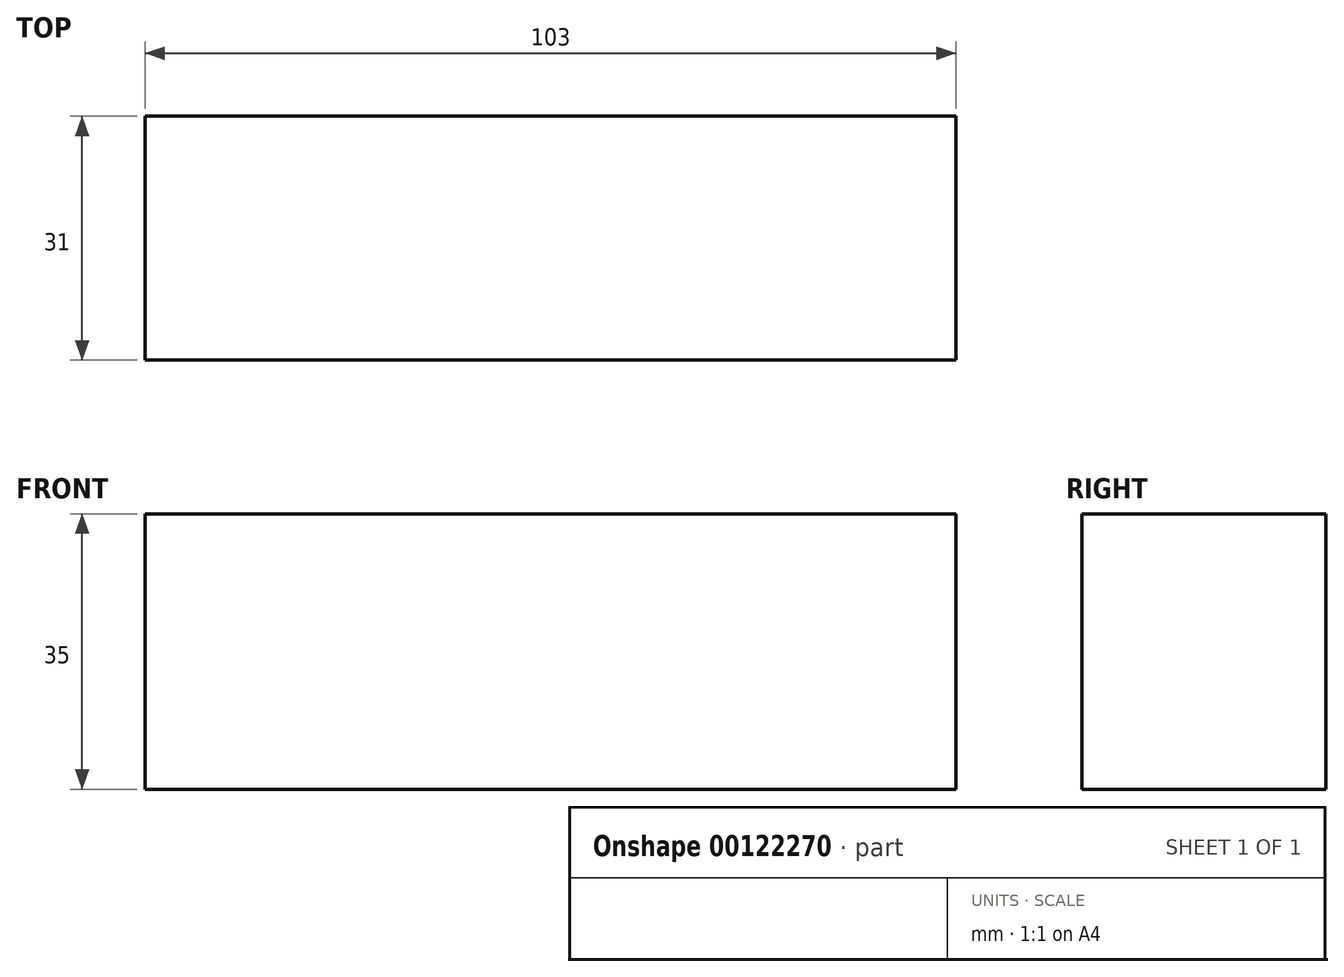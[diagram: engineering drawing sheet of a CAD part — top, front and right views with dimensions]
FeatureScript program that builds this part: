
annotation { "Feature Type Name" : "Feature", "Feature Type Description" : "" }
export const myFeature = defineFeature(function(context is Context, id is Id, definition is map)
    precondition{}
    {
        {
            var Q0;
            Q0=qCreatedBy(makeId("Front.planeOp"),FACE);
            var sketch = newSketch(context, id + "F0", { "sketchPlane" : qUnion([Q0])});
            skLineSegment(sketch, "E0.bottom", {"start": v(-51.47, 35) * mm, "end": v(51.53, 35) * mm});
            skLineSegment(sketch, "E0.top", {"start": v(-51.47, 0) * mm, "end": v(51.53, 0) * mm});
            skLineSegment(sketch, "E0.left", {"start": v(-51.47, 35) * mm, "end": v(-51.47, 0) * mm});
            skLineSegment(sketch, "E0.right", {"start": v(51.53, 35) * mm, "end": v(51.53, 0) * mm});
            skSolve(sketch);
        }
        {
            var Q0;
            Q0=makeQuery(id+"F0.imprint","IMPRINT",FACE,{"disambiguationData":[TD([[makeQuery(id+"F0.imprint","IMPRINT",EDGE,{"derivedFrom":sQuery(id+"F0.wireOp",EDGE,"E0.bottom")}),-1.0]])]});
            extrude(context, id + "F1", {"entities" : qUnion([Q0]), "depth" : 31 * mm});
        }
    });
